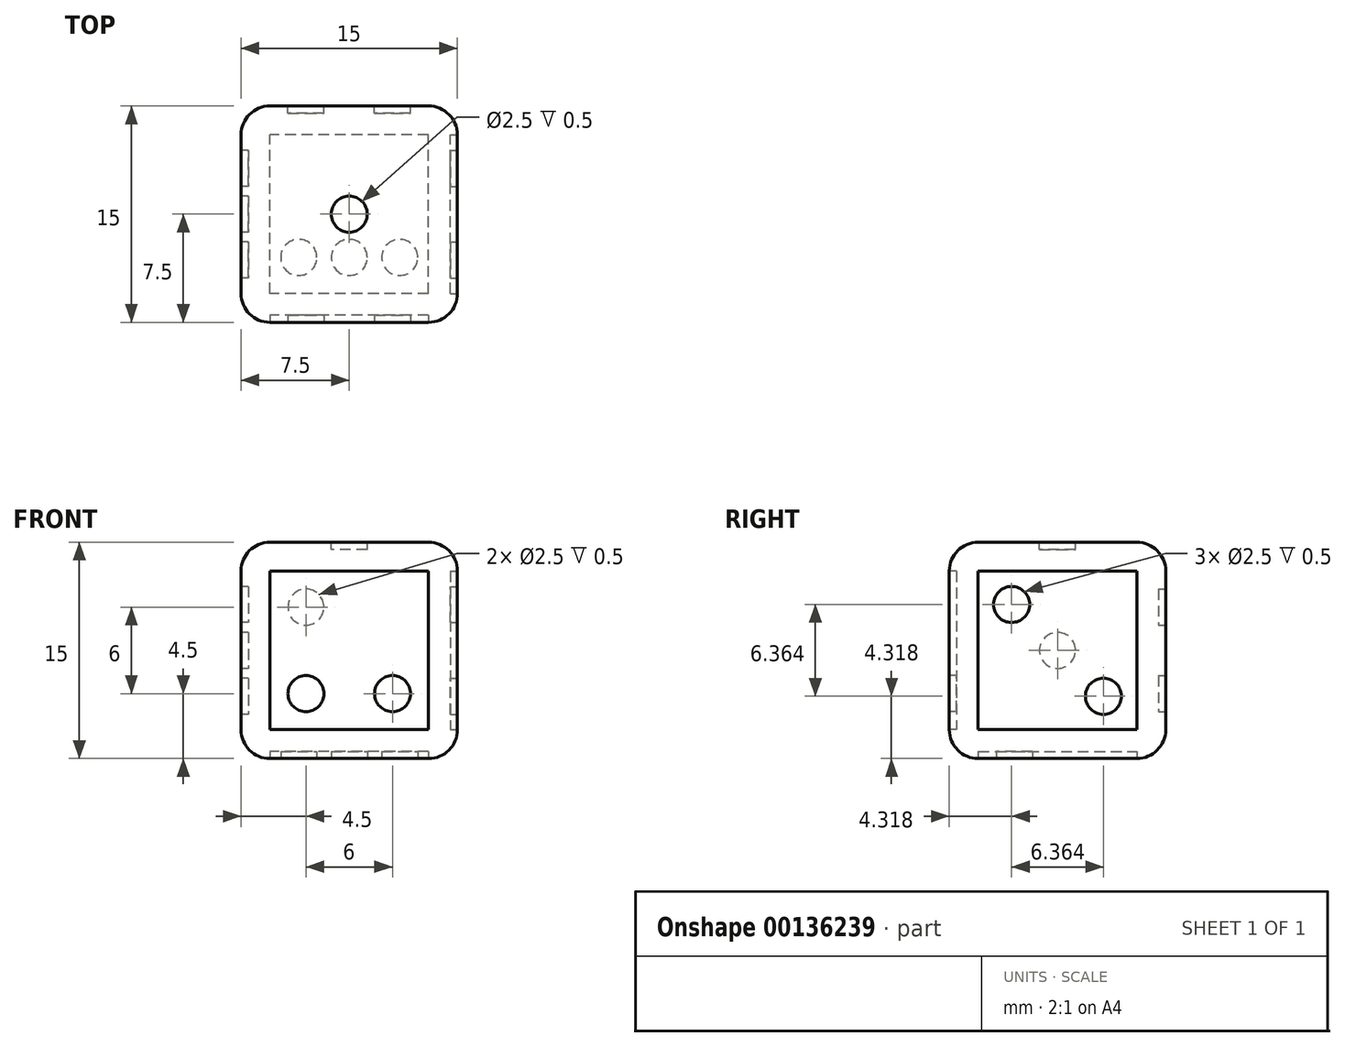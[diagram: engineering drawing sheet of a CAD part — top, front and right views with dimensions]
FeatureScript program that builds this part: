
annotation { "Feature Type Name" : "Feature", "Feature Type Description" : "" }
export const myFeature = defineFeature(function(context is Context, id is Id, definition is map)
    precondition{}
    {
        {
            var Q0;
            Q0=qCreatedBy(makeId("Top.planeOp"),FACE);
            var sketch = newSketch(context, id + "F0", { "sketchPlane" : qUnion([Q0])});
            skLineSegment(sketch, "E0.bottom", {"start": v(0, 0) * mm, "end": v(-15, 0) * mm});
            skLineSegment(sketch, "E0.top", {"start": v(0, 15) * mm, "end": v(-15, 15) * mm});
            skLineSegment(sketch, "E0.left", {"start": v(0, 0) * mm, "end": v(0, 15) * mm});
            skLineSegment(sketch, "E0.right", {"start": v(-15, 0) * mm, "end": v(-15, 15) * mm});
            skSolve(sketch);
        }
        {
            var Q0;
            Q0=makeQuery(id+"F0.imprint","IMPRINT",FACE,{"disambiguationData":[TD([[makeQuery(id+"F0.imprint","IMPRINT",EDGE,{"derivedFrom":sQuery(id+"F0.wireOp",EDGE,"E0.bottom")}),-1.0]])]});
            extrude(context, id + "F1", {"entities" : qUnion([Q0]), "depth" : 15 * mm});
        }
        {
            var Q0;
            Q0=makeQuery(id+"F1.opExtrude","SWEPT_EDGE",EDGE,{"disambiguationData":[OSD([sQuery(id+"F0.wireOp",EDGE,"E0.top"),sQuery(id+"F0.wireOp",EDGE,"E0.right")])]});
            var Q1;
            Q1=makeQuery(id+"F1.opExtrude","SWEPT_EDGE",EDGE,{"disambiguationData":[OSD([sQuery(id+"F0.wireOp",EDGE,"E0.top"),sQuery(id+"F0.wireOp",EDGE,"E0.left")])]});
            var Q2;
            Q2=makeQuery(id+"F1.opExtrude","SWEPT_EDGE",EDGE,{"disambiguationData":[OSD([sQuery(id+"F0.wireOp",EDGE,"E0.bottom"),sQuery(id+"F0.wireOp",EDGE,"E0.left")])]});
            var Q3;
            Q3=makeQuery(id+"F1.opExtrude","CAP_EDGE",EDGE,{"disambiguationData":[OSD([sQuery(id+"F0.wireOp",EDGE,"E0.bottom")])],"isStart":false});
            var Q4;
            Q4=makeQuery(id+"F1.opExtrude","CAP_EDGE",EDGE,{"disambiguationData":[OSD([sQuery(id+"F0.wireOp",EDGE,"E0.top")])],"isStart":true});
            var Q5;
            Q5=makeQuery(id+"F1.opExtrude","CAP_EDGE",EDGE,{"disambiguationData":[OSD([sQuery(id+"F0.wireOp",EDGE,"E0.top")])],"isStart":false});
            var Q6;
            Q6=makeQuery(id+"F1.opExtrude","SWEPT_EDGE",EDGE,{"disambiguationData":[OSD([sQuery(id+"F0.wireOp",EDGE,"E0.bottom"),sQuery(id+"F0.wireOp",EDGE,"E0.right")])]});
            var Q7;
            Q7=makeQuery(id+"F1.opExtrude","CAP_EDGE",EDGE,{"disambiguationData":[OSD([sQuery(id+"F0.wireOp",EDGE,"E0.bottom")])],"isStart":true});
            var Q8;
            Q8=makeQuery(id+"F1.opExtrude","CAP_EDGE",EDGE,{"disambiguationData":[OSD([sQuery(id+"F0.wireOp",EDGE,"E0.left")])],"isStart":true});
            var Q9;
            Q9=makeQuery(id+"F1.opExtrude","CAP_EDGE",EDGE,{"disambiguationData":[OSD([sQuery(id+"F0.wireOp",EDGE,"E0.left")])],"isStart":false});
            var Q10;
            Q10=makeQuery(id+"F1.opExtrude","CAP_EDGE",EDGE,{"disambiguationData":[OSD([sQuery(id+"F0.wireOp",EDGE,"E0.right")])],"isStart":true});
            var Q11;
            Q11=makeQuery(id+"F1.opExtrude","CAP_EDGE",EDGE,{"disambiguationData":[OSD([sQuery(id+"F0.wireOp",EDGE,"E0.right")])],"isStart":false});
            fillet(context, id + "F2", {"entities" : qUnion([Q0, Q1, Q2, Q3, Q4, Q5, Q6, Q7, Q8, Q9, Q10, Q11]), "radius" : 2 * mm, "tangentPropagation" : true, "allowEdgeOverflow" : false});
        }
        {
            var Q0;
            Q0=makeQuery(id+"F1.opExtrude","CAP_FACE",FACE,{"disambiguationData":[OSD([sQuery(id+"F0.wireOp",EDGE,"E0.bottom"),sQuery(id+"F0.wireOp",EDGE,"E0.top"),sQuery(id+"F0.wireOp",EDGE,"E0.left"),sQuery(id+"F0.wireOp",EDGE,"E0.right")])],"isStart":false});
            var sketch = newSketch(context, id + "F3", { "sketchPlane" : qUnion([Q0])});
            skCircle(sketch, "E1", {"center": v(-7.5, 7.5) * mm, "radius": 1.25 * mm});
            skSolve(sketch);
        }
        {
            var Q0;
            Q0=makeQuery(id+"F3.imprint","IMPRINT",FACE,{"disambiguationData":[TD([[makeQuery(id+"F3.imprint","IMPRINT",EDGE,{"derivedFrom":sQuery(id+"F3.wireOp",EDGE,"E1")}),1.0]])]});
            extrude(context, id + "F4", {"entities" : qUnion([Q0]), "operationType" : NewBodyOperationType.REMOVE, "oppositeDirection" : true, "depth" : 0.5 * mm});
        }
        {
            var Q0;
            Q0=makeQuery(id+"F1.opExtrude","CAP_FACE",FACE,{"disambiguationData":[OSD([sQuery(id+"F0.wireOp",EDGE,"E0.bottom"),sQuery(id+"F0.wireOp",EDGE,"E0.top"),sQuery(id+"F0.wireOp",EDGE,"E0.left"),sQuery(id+"F0.wireOp",EDGE,"E0.right")])],"isStart":true});
            var sketch = newSketch(context, id + "F5", { "sketchPlane" : qUnion([Q0])});
            skLineSegment(sketch, "E2", {"start": v(-2, -10.5) * mm, "end": v(-13, -10.5) * mm, "construction": true});
            skCircle(sketch, "E3", {"center": v(-11, -10.5) * mm, "radius": 1.25 * mm});
            skCircle(sketch, "E4", {"center": v(-4, -10.5) * mm, "radius": 1.25 * mm});
            skCircle(sketch, "E5", {"center": v(-7.5, -10.5) * mm, "radius": 1.25 * mm});
            skLineSegment(sketch, "E6", {"start": v(-13, -7.5) * mm, "end": v(-2, -7.5) * mm, "construction": true});
            skLineSegment(sketch, "E7.MirrorCS", {"start": v(-2, -4.5) * mm, "end": v(-13, -4.5) * mm, "construction": true});
            skCircle(sketch, "E8.MirrorC", {"center": v(-11, -4.5) * mm, "radius": 1.25 * mm});
            skCircle(sketch, "E9.MirrorC", {"center": v(-7.5, -4.5) * mm, "radius": 1.25 * mm});
            skCircle(sketch, "E10.MirrorC", {"center": v(-4, -4.5) * mm, "radius": 1.25 * mm});
            skSolve(sketch);
        }
        {
            var Q0;
            Q0=makeQuery(id+"F1.opExtrude","SWEPT_FACE",FACE,{"disambiguationData":[OSD([sQuery(id+"F0.wireOp",EDGE,"E0.bottom")])]});
            var sketch = newSketch(context, id + "F6", { "sketchPlane" : qUnion([Q0])});
            skLineSegment(sketch, "E11", {"start": v(-13, 10.5) * mm, "end": v(-2, 10.5) * mm, "construction": true});
            skLineSegment(sketch, "E12", {"start": v(-13, 7.5) * mm, "end": v(-2, 7.5) * mm, "construction": true});
            skCircle(sketch, "E13", {"center": v(-10.5, 10.5) * mm, "radius": 1.25 * mm});
            skCircle(sketch, "E14", {"center": v(-4.5, 10.5) * mm, "radius": 1.25 * mm});
            skLineSegment(sketch, "E15.MirrorCS", {"start": v(-13, 4.5) * mm, "end": v(-2, 4.5) * mm, "construction": true});
            skCircle(sketch, "E16.MirrorC", {"center": v(-10.5, 4.5) * mm, "radius": 1.25 * mm});
            skCircle(sketch, "E17.MirrorC", {"center": v(-4.5, 4.5) * mm, "radius": 1.25 * mm});
            skSolve(sketch);
        }
        {
            var Q0;
            Q0=makeQuery(id+"F1.opExtrude","SWEPT_FACE",FACE,{"disambiguationData":[OSD([sQuery(id+"F0.wireOp",EDGE,"E0.right")])]});
            var sketch = newSketch(context, id + "F7", { "sketchPlane" : qUnion([Q0])});
            skLineSegment(sketch, "E18", {"start": v(-13, 2) * mm, "end": v(-2, 13) * mm, "construction": true});
            skCircle(sketch, "E19", {"center": v(-4.32, 10.68) * mm, "radius": 1.25 * mm});
            skCircle(sketch, "E20", {"center": v(-7.5, 7.5) * mm, "radius": 1.25 * mm});
            skCircle(sketch, "E21", {"center": v(-10.68, 4.32) * mm, "radius": 1.25 * mm});
            skSolve(sketch);
        }
        {
            var Q0;
            Q0=makeQuery(id+"F7.imprint","IMPRINT",FACE,{"disambiguationData":[TD([[makeQuery(id+"F7.imprint","IMPRINT",EDGE,{"derivedFrom":sQuery(id+"F7.wireOp",EDGE,"E21")}),1.0]])]});
            var Q1;
            Q1=makeQuery(id+"F7.imprint","IMPRINT",FACE,{"disambiguationData":[TD([[makeQuery(id+"F7.imprint","IMPRINT",EDGE,{"derivedFrom":sQuery(id+"F7.wireOp",EDGE,"E20")}),1.0]])]});
            var Q2;
            Q2=makeQuery(id+"F7.imprint","IMPRINT",FACE,{"disambiguationData":[TD([[makeQuery(id+"F7.imprint","IMPRINT",EDGE,{"derivedFrom":sQuery(id+"F7.wireOp",EDGE,"E19")}),1.0]])]});
            extrude(context, id + "F8", {"entities" : qUnion([Q0, Q1, Q2]), "operationType" : NewBodyOperationType.ADD, "depth" : 0.5 * mm});
        }
        {
            var Q0;
            Q0=makeQuery(id+"F8.opExtrude","CAP_FACE",FACE,{"disambiguationData":[OSD([sQuery(id+"F7.wireOp",EDGE,"E21")])],"isStart":false});
            var Q1;
            Q1=makeQuery(id+"F8.opExtrude","CAP_FACE",FACE,{"disambiguationData":[OSD([sQuery(id+"F7.wireOp",EDGE,"E20")])],"isStart":false});
            var Q2;
            Q2=makeQuery(id+"F8.opExtrude","CAP_FACE",FACE,{"disambiguationData":[OSD([sQuery(id+"F7.wireOp",EDGE,"E19")])],"isStart":false});
            extrude(context, id + "F9", {"entities" : qUnion([Q0, Q1, Q2]), "operationType" : NewBodyOperationType.REMOVE, "oppositeDirection" : true, "depth" : 1 * mm});
        }
        {
            var Q0;
            Q0=makeQuery(id+"F6.imprint","IMPRINT",FACE,{"disambiguationData":[TD([[makeQuery(id+"F6.imprint","IMPRINT",EDGE,{"derivedFrom":sQuery(id+"F6.wireOp",EDGE,"E17.MirrorC")}),-1.0]])]});
            var Q1;
            Q1=makeQuery(id+"F6.imprint","IMPRINT",FACE,{"disambiguationData":[TD([[makeQuery(id+"F6.imprint","IMPRINT",EDGE,{"derivedFrom":sQuery(id+"F6.wireOp",EDGE,"E16.MirrorC")}),-1.0]])]});
            var Q2;
            Q2=makeQuery(id+"F6.imprint","IMPRINT",FACE,{"disambiguationData":[TD([[makeQuery(id+"F6.imprint","IMPRINT",EDGE,{"derivedFrom":sQuery(id+"F6.wireOp",EDGE,"E13")}),1.0]])]});
            var Q3;
            Q3=makeQuery(id+"F6.imprint","IMPRINT",FACE,{"disambiguationData":[TD([[makeQuery(id+"F6.imprint","IMPRINT",EDGE,{"derivedFrom":sQuery(id+"F6.wireOp",EDGE,"E14")}),1.0]])]});
            extrude(context, id + "F10", {"entities" : qUnion([Q0, Q1, Q2, Q3]), "operationType" : NewBodyOperationType.REMOVE, "oppositeDirection" : true, "depth" : 0.5 * mm});
        }
        {
            var Q0;
            Q0=makeQuery(id+"F1.opExtrude","SWEPT_FACE",FACE,{"disambiguationData":[OSD([sQuery(id+"F0.wireOp",EDGE,"E0.left")])]});
            var sketch = newSketch(context, id + "F11", { "sketchPlane" : qUnion([Q0])});
            skLineSegment(sketch, "E22", {"start": v(2, 2) * mm, "end": v(13, 13) * mm, "construction": true});
            skCircle(sketch, "E23", {"center": v(10.68, 10.68) * mm, "radius": 1.25 * mm});
            skCircle(sketch, "E24", {"center": v(7.5, 7.5) * mm, "radius": 1.25 * mm});
            skCircle(sketch, "E25", {"center": v(4.32, 4.32) * mm, "radius": 1.25 * mm});
            skLineSegment(sketch, "E26", {"start": v(2, 7.5) * mm, "end": v(13, 7.5) * mm, "construction": true});
            skCircle(sketch, "E27.MirrorC", {"center": v(10.68, 4.32) * mm, "radius": 1.25 * mm});
            skCircle(sketch, "E28.MirrorC", {"center": v(4.32, 10.68) * mm, "radius": 1.25 * mm});
            skSolve(sketch);
        }
        {
            var Q0;
            Q0=makeQuery(id+"F11.imprint","IMPRINT",FACE,{"disambiguationData":[TD([[makeQuery(id+"F11.imprint","IMPRINT",EDGE,{"derivedFrom":sQuery(id+"F11.wireOp",EDGE,"E28.MirrorC")}),-1.0]])]});
            var Q1;
            Q1=makeQuery(id+"F11.imprint","IMPRINT",FACE,{"disambiguationData":[TD([[makeQuery(id+"F11.imprint","IMPRINT",EDGE,{"derivedFrom":sQuery(id+"F11.wireOp",EDGE,"E23")}),1.0]])]});
            var Q2;
            Q2=makeQuery(id+"F11.imprint","IMPRINT",FACE,{"disambiguationData":[TD([[makeQuery(id+"F11.imprint","IMPRINT",EDGE,{"derivedFrom":sQuery(id+"F11.wireOp",EDGE,"E24")}),1.0]])]});
            var Q3;
            Q3=makeQuery(id+"F11.imprint","IMPRINT",FACE,{"disambiguationData":[TD([[makeQuery(id+"F11.imprint","IMPRINT",EDGE,{"derivedFrom":sQuery(id+"F11.wireOp",EDGE,"E25")}),1.0]])]});
            var Q4;
            Q4=makeQuery(id+"F11.imprint","IMPRINT",FACE,{"disambiguationData":[TD([[makeQuery(id+"F11.imprint","IMPRINT",EDGE,{"derivedFrom":sQuery(id+"F11.wireOp",EDGE,"E27.MirrorC")}),-1.0]])]});
            extrude(context, id + "F12", {"entities" : qUnion([Q0, Q1, Q2, Q3, Q4]), "operationType" : NewBodyOperationType.REMOVE, "oppositeDirection" : true, "depth" : 0.5 * mm});
        }
        {
            var Q0;
            Q0=makeQuery(id+"F5.imprint","IMPRINT",FACE,{"disambiguationData":[TD([[makeQuery(id+"F5.imprint","IMPRINT",EDGE,{"derivedFrom":sQuery(id+"F5.wireOp",EDGE,"E8.MirrorC")}),-1.0]])]});
            var Q1;
            Q1=makeQuery(id+"F5.imprint","IMPRINT",FACE,{"disambiguationData":[TD([[makeQuery(id+"F5.imprint","IMPRINT",EDGE,{"derivedFrom":sQuery(id+"F5.wireOp",EDGE,"E9.MirrorC")}),-1.0]])]});
            var Q2;
            Q2=makeQuery(id+"F5.imprint","IMPRINT",FACE,{"disambiguationData":[TD([[makeQuery(id+"F5.imprint","IMPRINT",EDGE,{"derivedFrom":sQuery(id+"F5.wireOp",EDGE,"E10.MirrorC")}),-1.0]])]});
            var Q3;
            Q3=makeQuery(id+"F5.imprint","IMPRINT",FACE,{"disambiguationData":[TD([[makeQuery(id+"F5.imprint","IMPRINT",EDGE,{"derivedFrom":sQuery(id+"F5.wireOp",EDGE,"E4")}),1.0]])]});
            var Q4;
            Q4=makeQuery(id+"F5.imprint","IMPRINT",FACE,{"disambiguationData":[TD([[makeQuery(id+"F5.imprint","IMPRINT",EDGE,{"derivedFrom":sQuery(id+"F5.wireOp",EDGE,"E5")}),1.0]])]});
            var Q5;
            Q5=makeQuery(id+"F5.imprint","IMPRINT",FACE,{"disambiguationData":[TD([[makeQuery(id+"F5.imprint","IMPRINT",EDGE,{"derivedFrom":sQuery(id+"F5.wireOp",EDGE,"E3")}),1.0]])]});
            extrude(context, id + "F13", {"entities" : qUnion([Q0, Q1, Q2, Q3, Q4, Q5]), "operationType" : NewBodyOperationType.REMOVE, "oppositeDirection" : true, "depth" : 0.5 * mm});
        }
        {
            var Q0;
            Q0=makeQuery(id+"F1.opExtrude","SWEPT_FACE",FACE,{"disambiguationData":[OSD([sQuery(id+"F0.wireOp",EDGE,"E0.top")])]});
            var sketch = newSketch(context, id + "F14", { "sketchPlane" : qUnion([Q0])});
            skLineSegment(sketch, "E29", {"start": v(13, 13) * mm, "end": v(2, 2) * mm, "construction": true});
            skCircle(sketch, "E30", {"center": v(10.5, 10.5) * mm, "radius": 1.25 * mm});
            skCircle(sketch, "E31", {"center": v(4.5, 4.5) * mm, "radius": 1.25 * mm});
            skSolve(sketch);
        }
        {
            var Q0;
            Q0=makeQuery(id+"F14.imprint","IMPRINT",FACE,{"disambiguationData":[TD([[makeQuery(id+"F14.imprint","IMPRINT",EDGE,{"derivedFrom":sQuery(id+"F14.wireOp",EDGE,"E30")}),1.0]])]});
            var Q1;
            Q1=makeQuery(id+"F14.imprint","IMPRINT",FACE,{"disambiguationData":[TD([[makeQuery(id+"F14.imprint","IMPRINT",EDGE,{"derivedFrom":sQuery(id+"F14.wireOp",EDGE,"E31")}),1.0]])]});
            extrude(context, id + "F15", {"entities" : qUnion([Q0, Q1]), "operationType" : NewBodyOperationType.REMOVE, "oppositeDirection" : true, "depth" : 0.5 * mm});
        }
    });
